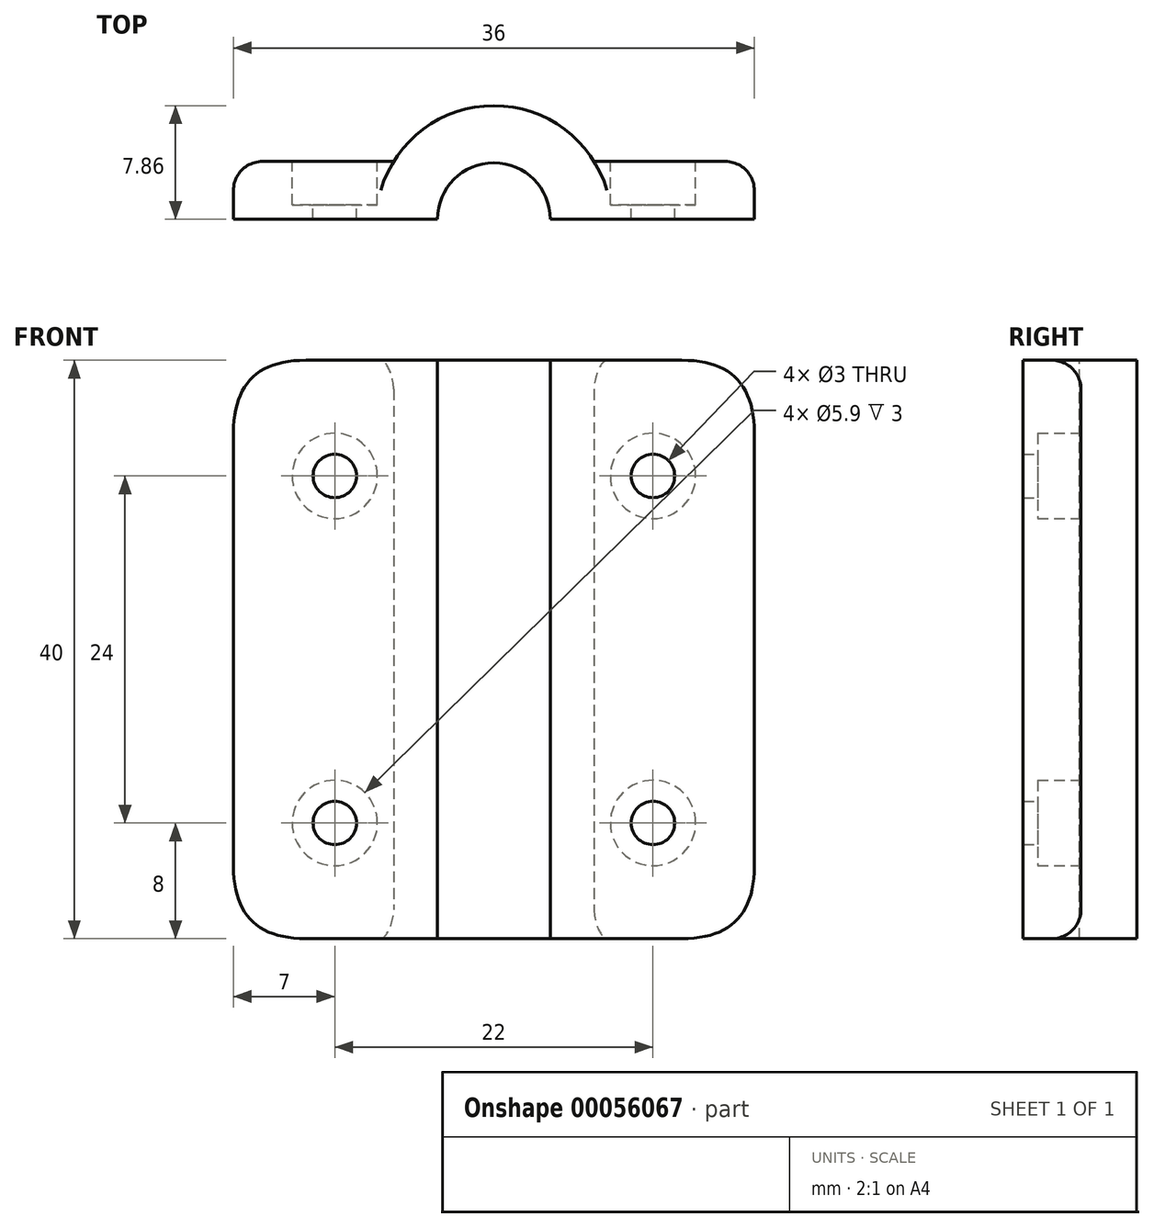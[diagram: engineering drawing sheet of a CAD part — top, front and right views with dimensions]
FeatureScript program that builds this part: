
annotation { "Feature Type Name" : "Feature", "Feature Type Description" : "" }
export const myFeature = defineFeature(function(context is Context, id is Id, definition is map)
    precondition{}
    {
        {
            var Q0;
            Q0=qCreatedBy(makeId("Top.planeOp"),FACE);
            var sketch = newSketch(context, id + "F0", { "sketchPlane" : qUnion([Q0])});
            skCircle(sketch, "E0", {"center": v(0, 0) * mm, "radius": 8 * mm, "construction": true});
            skLineSegment(sketch, "E1", {"start": v(0, 0) * mm, "end": v(18, 0) * mm});
            skLineSegment(sketch, "E2", {"start": v(0, 0) * mm, "end": v(-18, 0) * mm});
            skLineSegment(sketch, "E3", {"start": v(-18, 4) * mm, "end": v(-6.93, 4) * mm});
            skLineSegment(sketch, "E4", {"start": v(18, 4) * mm, "end": v(6.93, 4) * mm});
            skLineSegment(sketch, "E5", {"start": v(-18, 0) * mm, "end": v(-18, 4) * mm});
            skLineSegment(sketch, "E6", {"start": v(18, 0) * mm, "end": v(18, 4) * mm});
            skArc(sketch, "E7", {"start": v(6.93, 4) * mm, "mid": v(0, 7.86) * mm, "end": v(-6.93, 4) * mm});
            skSolve(sketch);
        }
        {
            var Q0;
            Q0 = qSketchRegion(id + "F0", true);
            extrude(context, id + "F1", {"entities" : qUnion([Q0]), "depth" : 40 * mm});
        }
        {
            var Q0;
            Q0=makeQuery(id+"F1.opExtrude","CAP_FACE",FACE,{"disambiguationData":[OSD([sQuery(id+"F0.wireOp",EDGE,"E1"),sQuery(id+"F0.wireOp",EDGE,"E2"),sQuery(id+"F0.wireOp",EDGE,"E3"),sQuery(id+"F0.wireOp",EDGE,"E4"),sQuery(id+"F0.wireOp",EDGE,"E5"),sQuery(id+"F0.wireOp",EDGE,"E6"),sQuery(id+"F0.wireOp",EDGE,"E7")])],"isStart":false});
            var sketch = newSketch(context, id + "F2", { "sketchPlane" : qUnion([Q0])});
            skCircle(sketch, "E8", {"center": v(0, 0) * mm, "radius": 3.9 * mm});
            skSolve(sketch);
        }
        {
            var Q0;
            {var subQ0=sQuery(id+"F2.wireOp",EDGE,"E8");var subQ1=makeQuery(id+"F1.opExtrude","CAP_EDGE",EDGE,{"disambiguationData":[OSD([sQuery(id+"F0.wireOp",EDGE,"E1"),sQuery(id+"F0.wireOp",EDGE,"E2")])],"isStart":false});var subQ2=makeQuery(id+"F2.imprint","INTERSECT",VERTEX,{"disambiguationData":[OD(0.0)],"derivedFrom":[subQ1,subQ0]});Q0=makeQuery(id+"F2.imprint","IMPRINT",FACE,{"disambiguationData":[TD([[makeQuery(id+"F2.imprint","IMPRINT",EDGE,{"disambiguationData":[TD([[subQ2,-1.0]])],"derivedFrom":subQ0}),1.0]])]});}
            extrude(context, id + "F3", {"entities" : qUnion([Q0]), "operationType" : NewBodyOperationType.REMOVE, "oppositeDirection" : true, "depth" : 40 * mm});
        }
        {
            var Q0;
            Q0=makeQuery(id+"F1.opExtrude","SWEPT_FACE",FACE,{"disambiguationData":[OSD([sQuery(id+"F0.wireOp",EDGE,"E3")])]});
            var sketch = newSketch(context, id + "F4", { "sketchPlane" : qUnion([Q0])});
            skCircle(sketch, "E9", {"center": v(11, 8) * mm, "radius": 1.5 * mm});
            skCircle(sketch, "E10", {"center": v(11, 32) * mm, "radius": 1.5 * mm});
            skCircle(sketch, "E11", {"center": v(-11, 8) * mm, "radius": 1.5 * mm});
            skCircle(sketch, "E12", {"center": v(-11, 32) * mm, "radius": 1.5 * mm});
            skSolve(sketch);
        }
        {
            var Q0;
            Q0=makeQuery(id+"F4.imprint","IMPRINT",FACE,{"disambiguationData":[TD([[makeQuery(id+"F4.imprint","IMPRINT",EDGE,{"derivedFrom":sQuery(id+"F4.wireOp",EDGE,"E11")}),1.0]])]});
            var Q1;
            Q1=makeQuery(id+"F4.imprint","IMPRINT",FACE,{"disambiguationData":[TD([[makeQuery(id+"F4.imprint","IMPRINT",EDGE,{"derivedFrom":sQuery(id+"F4.wireOp",EDGE,"E12")}),1.0]])]});
            var Q2;
            Q2=makeQuery(id+"F4.imprint","IMPRINT",FACE,{"disambiguationData":[TD([[makeQuery(id+"F4.imprint","IMPRINT",EDGE,{"derivedFrom":sQuery(id+"F4.wireOp",EDGE,"E10")}),1.0]])]});
            var Q3;
            Q3=makeQuery(id+"F4.imprint","IMPRINT",FACE,{"disambiguationData":[TD([[makeQuery(id+"F4.imprint","IMPRINT",EDGE,{"derivedFrom":sQuery(id+"F4.wireOp",EDGE,"E9")}),1.0]])]});
            extrude(context, id + "F5", {"entities" : qUnion([Q0, Q1, Q2, Q3]), "operationType" : NewBodyOperationType.REMOVE, "oppositeDirection" : true, "depth" : 25 * mm});
        }
        {
            var Q0;
            Q0=makeQuery(id+"F1.opExtrude","SWEPT_FACE",FACE,{"disambiguationData":[OSD([sQuery(id+"F0.wireOp",EDGE,"E4")])]});
            var sketch = newSketch(context, id + "F6", { "sketchPlane" : qUnion([Q0])});
            skCircle(sketch, "E13", {"center": v(-11, 8) * mm, "radius": 2.95 * mm});
            skCircle(sketch, "E14", {"center": v(-11, 32) * mm, "radius": 2.95 * mm});
            skCircle(sketch, "E15", {"center": v(11, 32) * mm, "radius": 2.95 * mm});
            skCircle(sketch, "E16", {"center": v(11, 8) * mm, "radius": 2.95 * mm});
            skSolve(sketch);
        }
        {
            var Q0;
            Q0=makeQuery(id+"F6.imprint","IMPRINT",FACE,{"disambiguationData":[TD([[makeQuery(id+"F6.imprint","IMPRINT",EDGE,{"derivedFrom":sQuery(id+"F6.wireOp",EDGE,"E14")}),1.0]])]});
            var Q1;
            Q1=makeQuery(id+"F6.imprint","IMPRINT",FACE,{"disambiguationData":[TD([[makeQuery(id+"F6.imprint","IMPRINT",EDGE,{"derivedFrom":sQuery(id+"F6.wireOp",EDGE,"E13")}),1.0]])]});
            var Q2;
            Q2=makeQuery(id+"F6.imprint","IMPRINT",FACE,{"disambiguationData":[TD([[makeQuery(id+"F6.imprint","IMPRINT",EDGE,{"derivedFrom":sQuery(id+"F6.wireOp",EDGE,"E16")}),1.0]])]});
            var Q3;
            Q3=makeQuery(id+"F6.imprint","IMPRINT",FACE,{"disambiguationData":[TD([[makeQuery(id+"F6.imprint","IMPRINT",EDGE,{"derivedFrom":sQuery(id+"F6.wireOp",EDGE,"E15")}),1.0]])]});
            extrude(context, id + "F7", {"entities" : qUnion([Q0, Q1, Q2, Q3]), "operationType" : NewBodyOperationType.REMOVE, "oppositeDirection" : true, "depth" : 3 * mm});
        }
        {
            var Q0;
            Q0=makeQuery(id+"F1.opExtrude","CAP_EDGE",EDGE,{"disambiguationData":[OSD([sQuery(id+"F0.wireOp",EDGE,"E6")])],"isStart":true});
            var Q1;
            Q1=makeQuery(id+"F1.opExtrude","CAP_EDGE",EDGE,{"disambiguationData":[OSD([sQuery(id+"F0.wireOp",EDGE,"E6")])],"isStart":false});
            var Q2;
            Q2=makeQuery(id+"F1.opExtrude","CAP_EDGE",EDGE,{"disambiguationData":[OSD([sQuery(id+"F0.wireOp",EDGE,"E5")])],"isStart":false});
            var Q3;
            Q3=makeQuery(id+"F1.opExtrude","CAP_EDGE",EDGE,{"disambiguationData":[OSD([sQuery(id+"F0.wireOp",EDGE,"E5")])],"isStart":true});
            fillet(context, id + "F8", {"entities" : qUnion([Q0, Q1, Q2, Q3]), "radius" : 5 * mm, "tangentPropagation" : true, "rho" : 0.5, "crossSection" : FilletCrossSection.CONIC, "allowEdgeOverflow" : false});
        }
        {
            var Q0;
            Q0=makeQuery(id+"F1.opExtrude","SWEPT_EDGE",EDGE,{"disambiguationData":[OSD([sQuery(id+"F0.wireOp",EDGE,"E3"),sQuery(id+"F0.wireOp",EDGE,"E5")])]});
            var Q1;
            Q1=makeQuery(id+"F1.opExtrude","SWEPT_EDGE",EDGE,{"disambiguationData":[OSD([sQuery(id+"F0.wireOp",EDGE,"E4"),sQuery(id+"F0.wireOp",EDGE,"E6")])]});
            fillet(context, id + "F9", {"entities" : qUnion([Q0, Q1]), "radius" : 2 * mm, "tangentPropagation" : true, "allowEdgeOverflow" : false});
        }
    });
